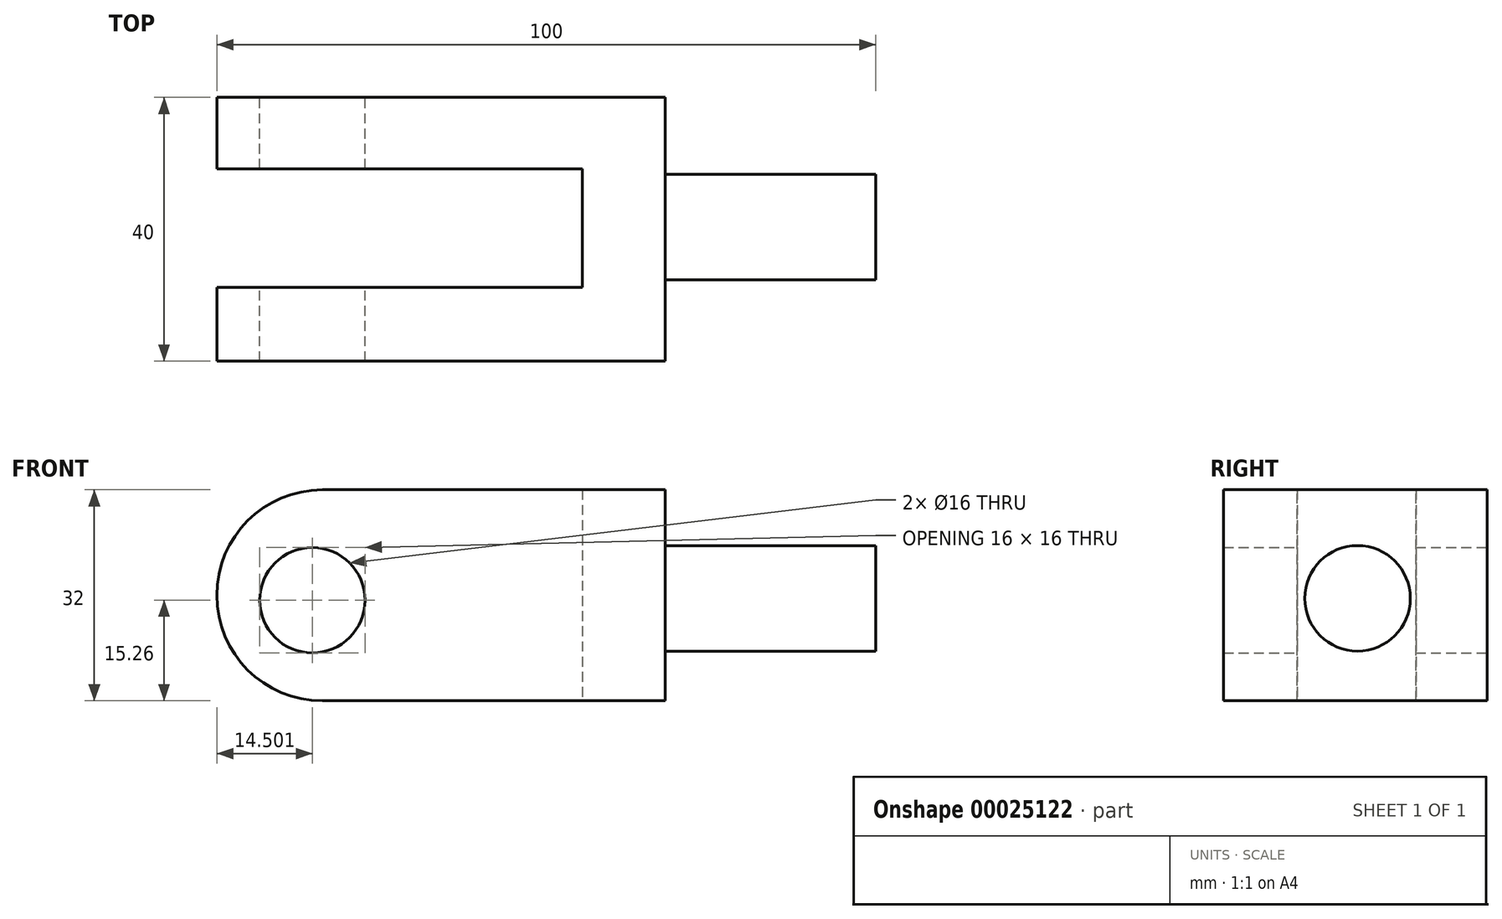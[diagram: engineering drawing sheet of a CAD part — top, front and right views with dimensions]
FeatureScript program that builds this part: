
annotation { "Feature Type Name" : "Feature", "Feature Type Description" : "" }
export const myFeature = defineFeature(function(context is Context, id is Id, definition is map)
    precondition{}
    {
        {
            var Q0;
            Q0=qCreatedBy(makeId("Front.planeOp"),FACE);
            var sketch = newSketch(context, id + "F0", { "sketchPlane" : qUnion([Q0])});
            skLineSegment(sketch, "E0", {"start": v(-27.3, 0) * mm, "end": v(24.7, 0) * mm});
            skLineSegment(sketch, "E1", {"start": v(24.7, 0) * mm, "end": v(24.7, 32) * mm});
            skLineSegment(sketch, "E2", {"start": v(24.7, 32) * mm, "end": v(-27.3, 32) * mm});
            skArc(sketch, "E3", {"start": v(-27.3, 32) * mm, "mid": v(-43.3, 16) * mm, "end": v(-27.3, 0) * mm});
            skSolve(sketch);
        }
        {
            var Q0;
            Q0=makeQuery(id+"F0.imprint","IMPRINT",FACE,{"disambiguationData":[TD([[makeQuery(id+"F0.imprint","IMPRINT",EDGE,{"derivedFrom":sQuery(id+"F0.wireOp",EDGE,"E0")}),1.0]])]});
            extrude(context, id + "F1", {"entities" : qUnion([Q0]), "depth" : 40 * mm});
        }
        {
            var Q0;
            Q0=qCreatedBy(makeId("Top.planeOp"),FACE);
            var sketch = newSketch(context, id + "F2", { "sketchPlane" : qUnion([Q0])});
            skLineSegment(sketch, "E4.bottom", {"start": v(-55.07, -10.83) * mm, "end": v(12.13, -10.83) * mm});
            skLineSegment(sketch, "E4.top", {"start": v(-55.07, -28.83) * mm, "end": v(12.13, -28.83) * mm});
            skLineSegment(sketch, "E4.left", {"start": v(-55.07, -10.83) * mm, "end": v(-55.07, -28.83) * mm});
            skLineSegment(sketch, "E4.right", {"start": v(12.13, -10.83) * mm, "end": v(12.13, -28.83) * mm});
            skSolve(sketch);
        }
        {
            var Q0;
            Q0=makeQuery(id+"F2.imprint","IMPRINT",FACE,{"disambiguationData":[TD([[makeQuery(id+"F2.imprint","IMPRINT",EDGE,{"derivedFrom":sQuery(id+"F2.wireOp",EDGE,"E4.bottom")}),-1.0]])]});
            extrude(context, id + "F3", {"entities" : qUnion([Q0]), "operationType" : NewBodyOperationType.REMOVE, "endBound" : BoundingType.THROUGH_ALL, "depth" : 25.4 * mm});
        }
        {
            var Q0;
            Q0=qCreatedBy(makeId("Front.planeOp"),FACE);
            var sketch = newSketch(context, id + "F4", { "sketchPlane" : qUnion([Q0])});
            skCircle(sketch, "E5", {"center": v(-28.8, 15.26) * mm, "radius": 8 * mm});
            skSolve(sketch);
        }
        {
            var Q0;
            Q0=makeQuery(id+"F4.imprint","IMPRINT",FACE,{"disambiguationData":[TD([[makeQuery(id+"F4.imprint","IMPRINT",EDGE,{"derivedFrom":sQuery(id+"F4.wireOp",EDGE,"E5")}),1.0]])]});
            var Q1;
            Q1=sQuery(id+"F4.wireOp",EDGE,"E5");
            extrude(context, id + "F5", {"entities" : qUnion([Q0]), "operationType" : NewBodyOperationType.REMOVE, "surfaceEntities" : qUnion([Q1]), "endBound" : BoundingType.THROUGH_ALL, "depth" : 25.4 * mm});
        }
        {
            var Q0;
            Q0=makeQuery(id+"F1.opExtrude","SWEPT_FACE",FACE,{"disambiguationData":[OSD([sQuery(id+"F0.wireOp",EDGE,"E1")])]});
            var sketch = newSketch(context, id + "F6", { "sketchPlane" : qUnion([Q0])});
            skCircle(sketch, "E6", {"center": v(-19.68, 15.55) * mm, "radius": 8 * mm});
            skSolve(sketch);
        }
        {
            var Q0;
            Q0=makeQuery(id+"F6.imprint","IMPRINT",FACE,{"disambiguationData":[TD([[makeQuery(id+"F6.imprint","IMPRINT",EDGE,{"derivedFrom":sQuery(id+"F6.wireOp",EDGE,"E6")}),1.0]])]});
            extrude(context, id + "F7", {"entities" : qUnion([Q0]), "operationType" : NewBodyOperationType.ADD, "depth" : 32 * mm});
        }
    });
